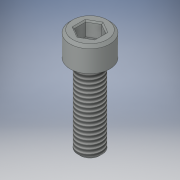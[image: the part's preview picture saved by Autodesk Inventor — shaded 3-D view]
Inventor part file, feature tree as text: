
AUTODESK INVENTOR PART (.ipt)
format: ipt  version: 2017.1 (Build 211199000, 199)  size: 122,880 bytes
history: native  units: in
note: dims shown in document units (in); Inventor stores cm internally (conversion verified against a paired STEP export)
features: thread x1, imported_body x1
ambient origin geometry x8: Origin, YZ Plane, XZ Plane, XY Plane, X Axis, Y Axis, Z Axis, Center Point
bodies: Solid1 (feature_tree)
feature tree (2):
  thread  "Thread1"  [1 undecoded]
  imported_body  "Imported1"
note: 1 required parameter value undecoded (feature->parameter linkage not recoverable at this tier; creation-order binding heuristic only, values carry confidence <= 0.55)
